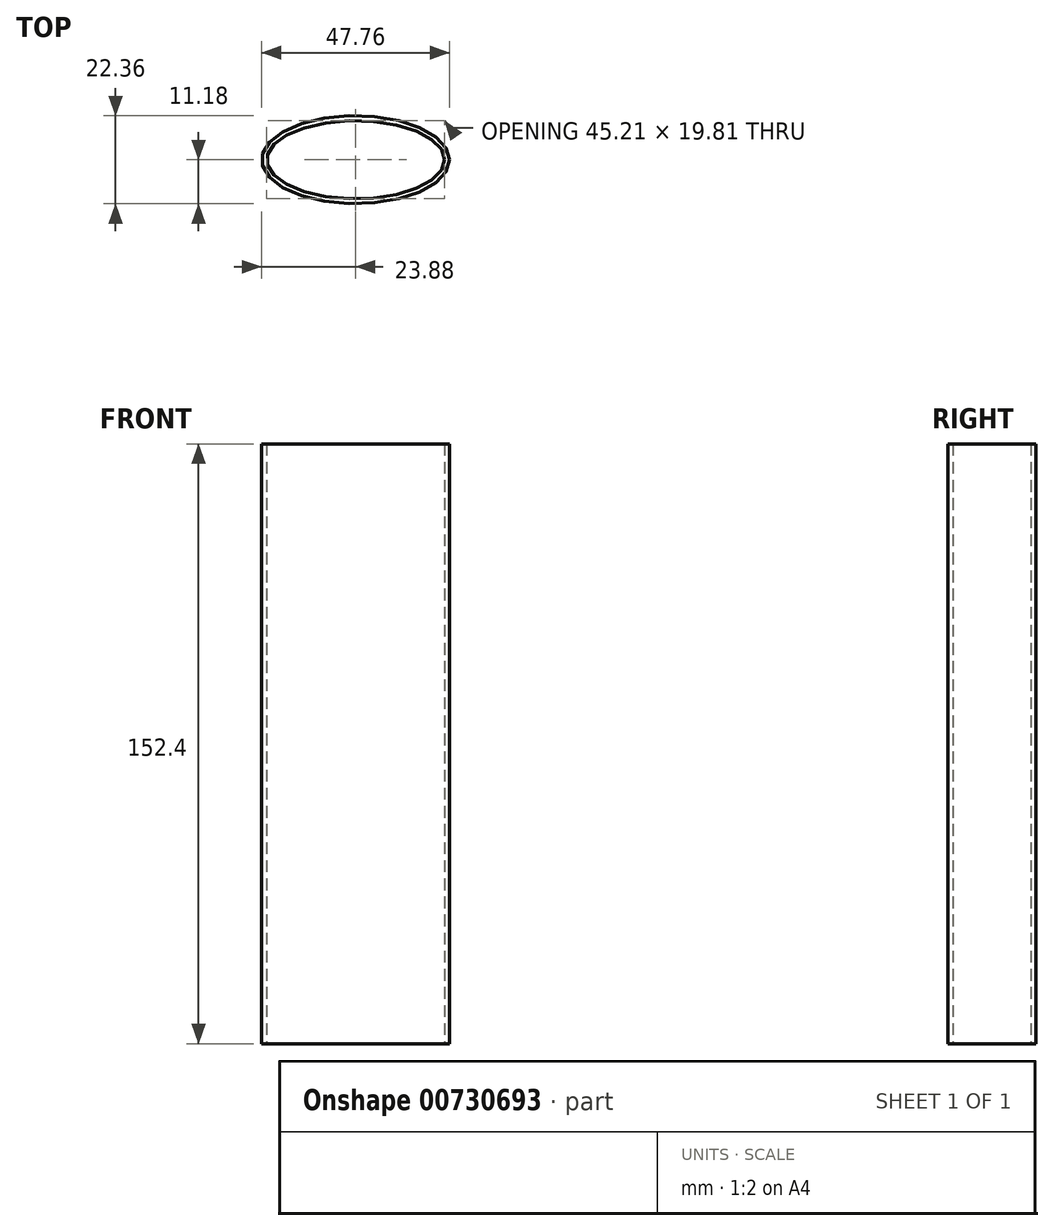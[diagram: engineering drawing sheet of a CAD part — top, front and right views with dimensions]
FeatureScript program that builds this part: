
annotation { "Feature Type Name" : "Feature", "Feature Type Description" : "" }
export const myFeature = defineFeature(function(context is Context, id is Id, definition is map)
    precondition{}
    {
        {
            var Q0;
            Q0=qCreatedBy(makeId("Top.planeOp"),FACE);
            var sketch = newSketch(context, id + "F0", { "sketchPlane" : qUnion([Q0])});
            skEllipse(sketch, "E0", {"center": v(0, 0) * mm, "majorRadius": 23.88 * mm, "minorRadius": 11.18 * mm, "majorAxis": v(1, 0)});
            skEllipse(sketch, "E1", {"center": v(0, 0) * mm, "majorRadius": 22.6 * mm, "minorRadius": 9.9 * mm, "majorAxis": v(1, 0)});
            skSolve(sketch);
        }
        {
            var Q0;
            Q0=makeQuery(id+"F0.imprint","IMPRINT",FACE,{"disambiguationData":[TD([[makeQuery(id+"F0.imprint","IMPRINT",EDGE,{"derivedFrom":sQuery(id+"F0.wireOp",EDGE,"E0")}),1.0]])]});
            extrude(context, id + "F1", {"entities" : qUnion([Q0]), "depth" : 152.4 * mm, "offsetDistance" : 25.4 * mm});
        }
    });
